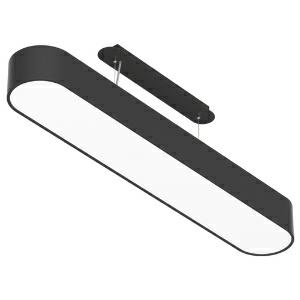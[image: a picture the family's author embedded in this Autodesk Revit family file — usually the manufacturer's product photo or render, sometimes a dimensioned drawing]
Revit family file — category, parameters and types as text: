
# Revit family: smoothline_1230x200_hl_led_38w_3040lm_3000k_cri80_410-1450
name_source: partatom
category: Leuchten
revit_build: Autodesk Revit 2016 (Build: 20190508_0715(x64)
units: mm (PartAtom-declared; Revit-internal decimal feet)

## family parameters
Basisbauteil = Fläche
Beim Laden mit Abzugskörper schneiden = Nein
Bemaßung runder Anschluss = Durchmesser verwenden
Gemeinsam genutzt = Nein
Lichtquelle = Nein
Raumberechnungspunkt = Nein
Teiletyp = Normal

## types (1)
- 410-1450-D01 (12 x LED, 429 lm, 3.2 W, 3000K)
    Approval mark = CE
    Beschreibung = The pendant luminaire SMOOTHLINE from the familiy SMOOTHY consists of aluminum-extruded profile. Charming SOFT-EDGE design ensure unparalleled styling. The ballast is integrated and allows for an operation with 220-240V (50/60Hz). SMOOTHLINE (# 410-1450) ist not dimmable (on/off). The luminaire with direct illumination and corresponds to protection class SK1 at IP20.
    CIE Flux Codes = 47 78 95 100 57
    Color Rendering = 1B/80…89
    Color Temperature = 3000K
    Height = 120 mm
    Hersteller = Prolicht
    Lamp Light Flux = 429 lm
    Lamp Power = 3.2 W
    Lamp count = 12
    Lampe = 12 x LED
    Length = 1230 mm
    Luminous efficacy = 76 lm/W
    ModVariant = Nein
    Modell = 410-1450
    Mounting Place = Ceiling
    Mounting Type = Pendant
    Number of Poles = 1
    OnlyDefault = Ja
    Power Factor = 1
    Product Name = SMOOTHLINE 1230x200 HL LED 38W 3040lm 3000K CRI80
    Product group = Suspended lights
    ProductGroupID = 941
    Protection Class = Protection class I
    Protection Degree = IP 20
    RLX_Detail_Level = 1
    RlxData = <blob elided: 38053 chars, md5=8e5b3bdc>
    Scheinlast = 38 VA
    Socket = socket
    Standby Power = 0 W
    System Light Flux = 2921 lm
    System Power = 38 W
    Typenbild = 410-1450.jpg
    URL = http://relux.com
    VarID = 410-1450-d01
    Voltage = 0 V
    Vorgabe-Ansicht = 1800 mm
    Weight = 0.00 kg
    Width = 200 mm  [stored 0.656168 ft]

note: [stored X ft] marks values corroborated as IEEE doubles in the binary element streams (Revit-internal decimal feet)

## geometry (parser evidence)
native form markers: Sweep x10
no freeform markers — native parametric forms only
